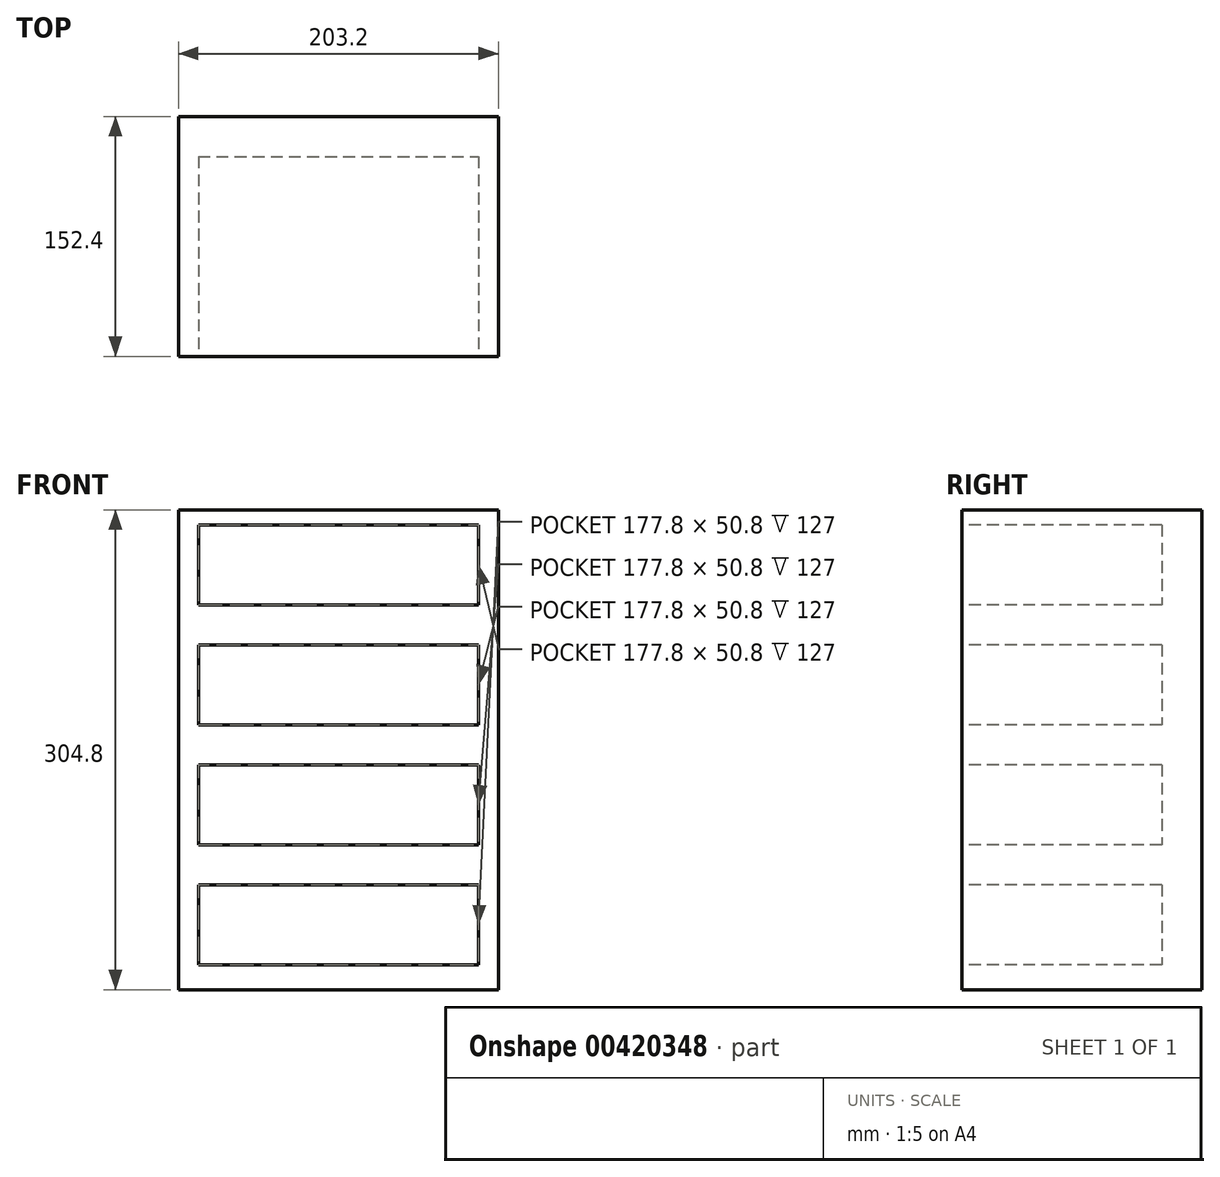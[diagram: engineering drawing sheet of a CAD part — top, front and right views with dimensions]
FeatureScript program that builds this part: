
annotation { "Feature Type Name" : "Feature", "Feature Type Description" : "" }
export const myFeature = defineFeature(function(context is Context, id is Id, definition is map)
    precondition{}
    {
        {
            var Q0;
            Q0=qCreatedBy(makeId("Top.planeOp"),FACE);
            var sketch = newSketch(context, id + "F0", { "sketchPlane" : qUnion([Q0])});
            skLineSegment(sketch, "E0.bottom", {"start": v(101.6, 76.2) * mm, "end": v(-101.6, 76.2) * mm});
            skLineSegment(sketch, "E0.top", {"start": v(101.6, -76.2) * mm, "end": v(-101.6, -76.2) * mm});
            skLineSegment(sketch, "E0.left", {"start": v(101.6, 76.2) * mm, "end": v(101.6, -76.2) * mm});
            skLineSegment(sketch, "E0.right", {"start": v(-101.6, 76.2) * mm, "end": v(-101.6, -76.2) * mm});
            skPoint(sketch, "E0.middle", {"position": v(0, 0) * mm});
            skSolve(sketch);
        }
        {
            var Q0;
            Q0=makeQuery(id+"F0.imprint","IMPRINT",FACE,{"disambiguationData":[TD([[makeQuery(id+"F0.imprint","IMPRINT",EDGE,{"derivedFrom":sQuery(id+"F0.wireOp",EDGE,"E0.bottom")}),1.0]])]});
            extrude(context, id + "F1", {"entities" : qUnion([Q0]), "depth" : 304.8 * mm});
        }
        {
            var Q0;
            Q0=makeQuery(id+"F1.opExtrude","SWEPT_FACE",FACE,{"disambiguationData":[OSD([sQuery(id+"F0.wireOp",EDGE,"E0.top")])]});
            var sketch = newSketch(context, id + "F2", { "sketchPlane" : qUnion([Q0])});
            skLineSegment(sketch, "E1.bottom", {"start": v(-88.9, 295.28) * mm, "end": v(88.9, 295.28) * mm});
            skLineSegment(sketch, "E1.top", {"start": v(-88.9, 244.48) * mm, "end": v(88.9, 244.48) * mm});
            skLineSegment(sketch, "E1.left", {"start": v(-88.9, 295.28) * mm, "end": v(-88.9, 244.48) * mm});
            skLineSegment(sketch, "E1.right", {"start": v(88.9, 295.28) * mm, "end": v(88.9, 244.48) * mm});
            skLineSegment(sketch, "E2.0.1.0", {"start": v(88.9, 219.07) * mm, "end": v(88.9, 168.28) * mm});
            skLineSegment(sketch, "E2.0.1.1", {"start": v(-88.9, 219.07) * mm, "end": v(88.9, 219.08) * mm});
            skLineSegment(sketch, "E2.0.1.2", {"start": v(-88.9, 219.07) * mm, "end": v(-88.9, 168.28) * mm});
            skLineSegment(sketch, "E2.0.1.3", {"start": v(-88.9, 168.28) * mm, "end": v(88.9, 168.28) * mm});
            skLineSegment(sketch, "E2.0.2.0", {"start": v(88.9, 142.87) * mm, "end": v(88.9, 92.08) * mm});
            skLineSegment(sketch, "E2.0.2.1", {"start": v(-88.9, 142.87) * mm, "end": v(88.9, 142.88) * mm});
            skLineSegment(sketch, "E2.0.2.2", {"start": v(-88.9, 142.87) * mm, "end": v(-88.9, 92.07) * mm});
            skLineSegment(sketch, "E2.0.2.3", {"start": v(-88.9, 92.08) * mm, "end": v(88.9, 92.08) * mm});
            skLineSegment(sketch, "E2.0.3.0", {"start": v(88.9, 66.67) * mm, "end": v(88.9, 15.88) * mm});
            skLineSegment(sketch, "E2.0.3.1", {"start": v(-88.9, 66.67) * mm, "end": v(88.9, 66.67) * mm});
            skLineSegment(sketch, "E2.0.3.2", {"start": v(-88.9, 66.67) * mm, "end": v(-88.9, 15.87) * mm});
            skLineSegment(sketch, "E2.0.3.3", {"start": v(-88.9, 15.87) * mm, "end": v(88.9, 15.88) * mm});
            skLineSegment(sketch, "E2.direction1", {"start": v(88.9, 241.3) * mm, "end": v(114.3, 241.3) * mm, "construction": true});
            skLineSegment(sketch, "E2.direction2", {"start": v(88.9, 241.3) * mm, "end": v(88.9, 165.1) * mm, "construction": true});
            skSolve(sketch);
        }
        {
            var Q0;
            Q0=makeQuery(id+"F2.imprint","IMPRINT",FACE,{"disambiguationData":[TD([[makeQuery(id+"F2.imprint","IMPRINT",EDGE,{"derivedFrom":sQuery(id+"F2.wireOp",EDGE,"E1.bottom")}),-1.0]])]});
            var Q1;
            Q1=makeQuery(id+"F2.imprint","IMPRINT",FACE,{"disambiguationData":[TD([[makeQuery(id+"F2.imprint","IMPRINT",EDGE,{"derivedFrom":sQuery(id+"F2.wireOp",EDGE,"E2.0.1.0")}),-1.0]])]});
            var Q2;
            Q2=makeQuery(id+"F2.imprint","IMPRINT",FACE,{"disambiguationData":[TD([[makeQuery(id+"F2.imprint","IMPRINT",EDGE,{"derivedFrom":sQuery(id+"F2.wireOp",EDGE,"E2.0.2.0")}),-1.0]])]});
            var Q3;
            Q3=makeQuery(id+"F2.imprint","IMPRINT",FACE,{"disambiguationData":[TD([[makeQuery(id+"F2.imprint","IMPRINT",EDGE,{"derivedFrom":sQuery(id+"F2.wireOp",EDGE,"E2.0.3.0")}),-1.0]])]});
            extrude(context, id + "F3", {"entities" : qUnion([Q0, Q1, Q2, Q3]), "operationType" : NewBodyOperationType.REMOVE, "oppositeDirection" : true, "depth" : 127 * mm});
        }
    });
